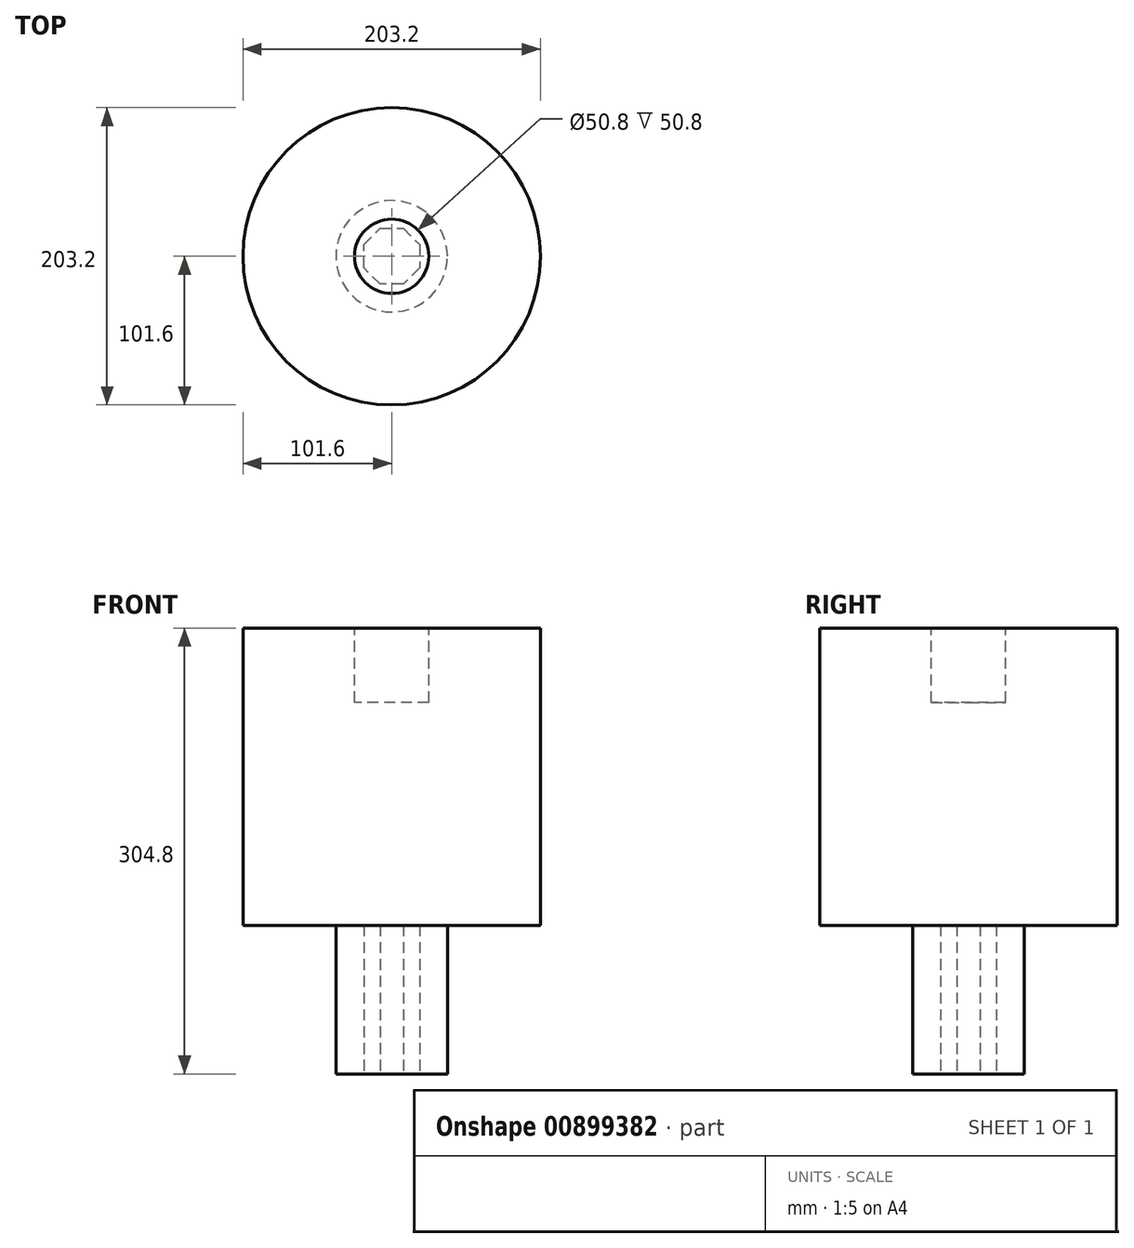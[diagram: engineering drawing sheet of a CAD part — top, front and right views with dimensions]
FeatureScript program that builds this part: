
annotation { "Feature Type Name" : "Feature", "Feature Type Description" : "" }
export const myFeature = defineFeature(function(context is Context, id is Id, definition is map)
    precondition{}
    {
        {
            var Q0;
            Q0=qCreatedBy(makeId("Top.planeOp"),FACE);
            var sketch = newSketch(context, id + "F0", { "sketchPlane" : qUnion([Q0])});
            skCircle(sketch, "E0", {"center": v(0, 0) * mm, "radius": 38.1 * mm});
            skCircle(sketch, "E1.cCircle", {"center": v(0, 0) * mm, "radius": 19.05 * mm, "construction": true});
            skLineSegment(sketch, "E1.0", {"start": v(-7.9, 19.05) * mm, "end": v(7.9, 19.05) * mm});
            skLineSegment(sketch, "E1.1", {"start": v(7.9, 19.05) * mm, "end": v(19.05, 7.9) * mm});
            skLineSegment(sketch, "E1.2", {"start": v(19.05, 7.9) * mm, "end": v(19.05, -7.9) * mm});
            skLineSegment(sketch, "E1.3", {"start": v(19.05, -7.9) * mm, "end": v(7.9, -19.05) * mm});
            skLineSegment(sketch, "E1.4", {"start": v(7.9, -19.05) * mm, "end": v(-7.9, -19.05) * mm});
            skLineSegment(sketch, "E1.5", {"start": v(-7.9, -19.05) * mm, "end": v(-19.05, -7.9) * mm});
            skLineSegment(sketch, "E1.6", {"start": v(-19.05, -7.9) * mm, "end": v(-19.05, 7.9) * mm});
            skLineSegment(sketch, "E1.7", {"start": v(-19.05, 7.9) * mm, "end": v(-7.9, 19.05) * mm});
            skPoint(sketch, "E1.0.midPoint", {"position": v(0, 19.05) * mm});
            skSolve(sketch);
        }
        {
            var Q0;
            Q0 = qSketchRegion(id + "F0", true);
            extrude(context, id + "F1", {"entities" : qUnion([Q0]), "depth" : 101.6 * mm, "offsetDistance" : 25.4 * mm});
        }
        {
            var Q0;
            Q0=makeQuery(id+"F1.opExtrude","CAP_FACE",FACE,{"disambiguationData":[OSD([sQuery(id+"F0.wireOp",EDGE,"E0"),sQuery(id+"F0.wireOp",EDGE,"E1.0"),sQuery(id+"F0.wireOp",EDGE,"E1.1"),sQuery(id+"F0.wireOp",EDGE,"E1.2"),sQuery(id+"F0.wireOp",EDGE,"E1.3"),sQuery(id+"F0.wireOp",EDGE,"E1.4"),sQuery(id+"F0.wireOp",EDGE,"E1.5"),sQuery(id+"F0.wireOp",EDGE,"E1.6"),sQuery(id+"F0.wireOp",EDGE,"E1.7")])],"isStart":false});
            var sketch = newSketch(context, id + "F2", { "sketchPlane" : qUnion([Q0])});
            skCircle(sketch, "E2", {"center": v(0, 0) * mm, "radius": 101.6 * mm});
            skSolve(sketch);
        }
        {
            var Q0;
            Q0=makeQuery(id+"F2.imprint","IMPRINT",FACE,{"disambiguationData":[TD([[makeQuery(id+"F2.imprint","IMPRINT",EDGE,{"derivedFrom":sQuery(id+"F2.wireOp",EDGE,"E2")}),1.0]])]});
            var Q1;
            Q1 = qSketchRegion(id + "F2", true);
            extrude(context, id + "F3", {"entities" : qUnion([Q0, Q1]), "operationType" : NewBodyOperationType.ADD, "depth" : 203.2 * mm, "offsetDistance" : 25.4 * mm});
        }
        {
            var Q0;
            Q0=makeQuery(id+"F3.opExtrude","CAP_FACE",FACE,{"disambiguationData":[OSD([sQuery(id+"F2.wireOp",EDGE,"E2")])],"isStart":false});
            var sketch = newSketch(context, id + "F4", { "sketchPlane" : qUnion([Q0])});
            skCircle(sketch, "E3", {"center": v(0, 0) * mm, "radius": 25.4 * mm});
            skSolve(sketch);
        }
        {
            var Q0;
            Q0 = qSketchRegion(id + "F4", true);
            extrude(context, id + "F5", {"entities" : qUnion([Q0]), "operationType" : NewBodyOperationType.REMOVE, "oppositeDirection" : true, "depth" : 50.8 * mm, "offsetDistance" : 25.4 * mm});
        }
    });
